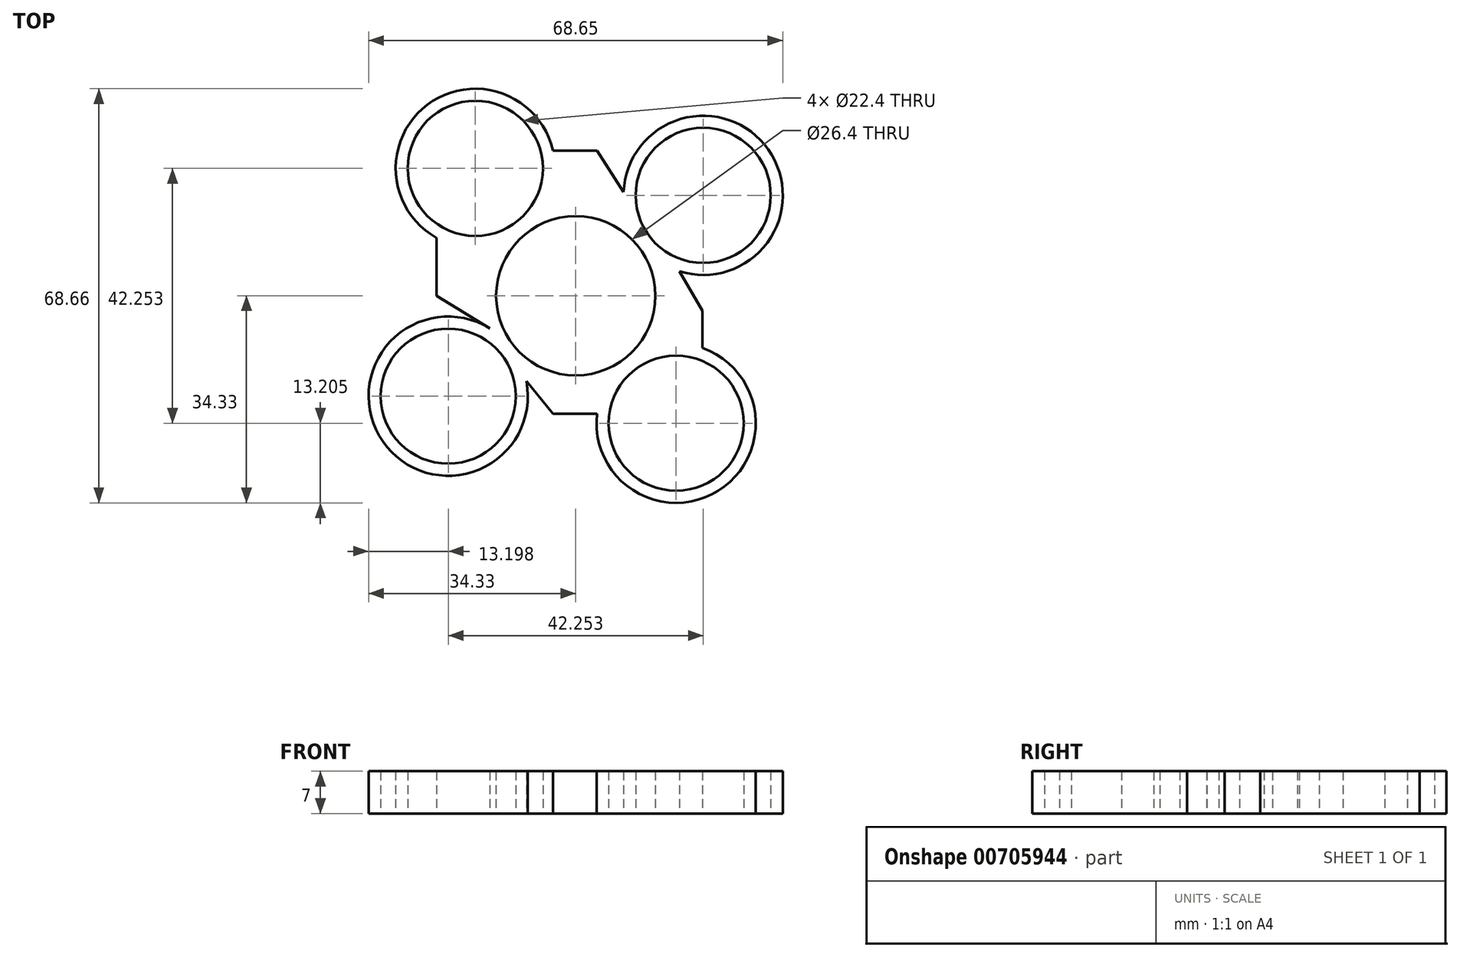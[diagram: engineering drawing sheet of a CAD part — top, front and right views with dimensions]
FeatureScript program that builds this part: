
annotation { "Feature Type Name" : "Feature", "Feature Type Description" : "" }
export const myFeature = defineFeature(function(context is Context, id is Id, definition is map)
    precondition{}
    {
        {
            var Q0;
            Q0=qCreatedBy(makeId("Top.planeOp"),FACE);
            var sketch = newSketch(context, id + "F0", { "sketchPlane" : qUnion([Q0])});
            skCircle(sketch, "E0", {"center": v(0, 0) * mm, "radius": 11.2 * mm});
            skCircle(sketch, "E1", {"center": v(0, 0) * mm, "radius": 13.2 * mm});
            skCircle(sketch, "E2", {"center": v(21.12, 16.65) * mm, "radius": 11.2 * mm});
            skCircle(sketch, "E3", {"center": v(21.12, 16.65) * mm, "radius": 13.2 * mm});
            skCircle(sketch, "E4.1.0", {"center": v(-16.65, 21.13) * mm, "radius": 13.2 * mm});
            skCircle(sketch, "E4.1.1", {"center": v(-16.65, 21.13) * mm, "radius": 11.2 * mm});
            skCircle(sketch, "E4.2.0", {"center": v(-21.13, -16.64) * mm, "radius": 13.2 * mm});
            skCircle(sketch, "E4.2.1", {"center": v(-21.13, -16.64) * mm, "radius": 11.2 * mm});
            skCircle(sketch, "E4.3.0", {"center": v(16.64, -21.13) * mm, "radius": 13.2 * mm});
            skCircle(sketch, "E4.3.1", {"center": v(16.64, -21.13) * mm, "radius": 11.2 * mm});
            skLineSegment(sketch, "E5", {"start": v(-8.16, -14.2) * mm, "end": v(-3.79, -19.54) * mm});
            skLineSegment(sketch, "E6", {"start": v(-3.79, -19.54) * mm, "end": v(3.54, -19.54) * mm});
            skLineSegment(sketch, "E7", {"start": v(20.99, -8.66) * mm, "end": v(20.99, -2.47) * mm});
            skLineSegment(sketch, "E8", {"start": v(20.99, -2.47) * mm, "end": v(17.16, 4.05) * mm});
            skLineSegment(sketch, "E9", {"start": v(-3.79, 24.1) * mm, "end": v(3.54, 24.1) * mm});
            skLineSegment(sketch, "E10", {"start": v(3.54, 24.1) * mm, "end": v(7.93, 17.18) * mm});
            skLineSegment(sketch, "E11", {"start": v(-23.08, 9.6) * mm, "end": v(-23.08, 0) * mm});
            skLineSegment(sketch, "E12", {"start": v(-23.08, 0) * mm, "end": v(-14.27, -5.37) * mm});
            skSolve(sketch);
        }
        {
            var Q0;
            Q0 = qSketchRegion(id + "F0", true);
            extrude(context, id + "F1", {"entities" : qUnion([Q0]), "depth" : 7 * mm, "offsetDistance" : 25 * mm});
        }
    });
